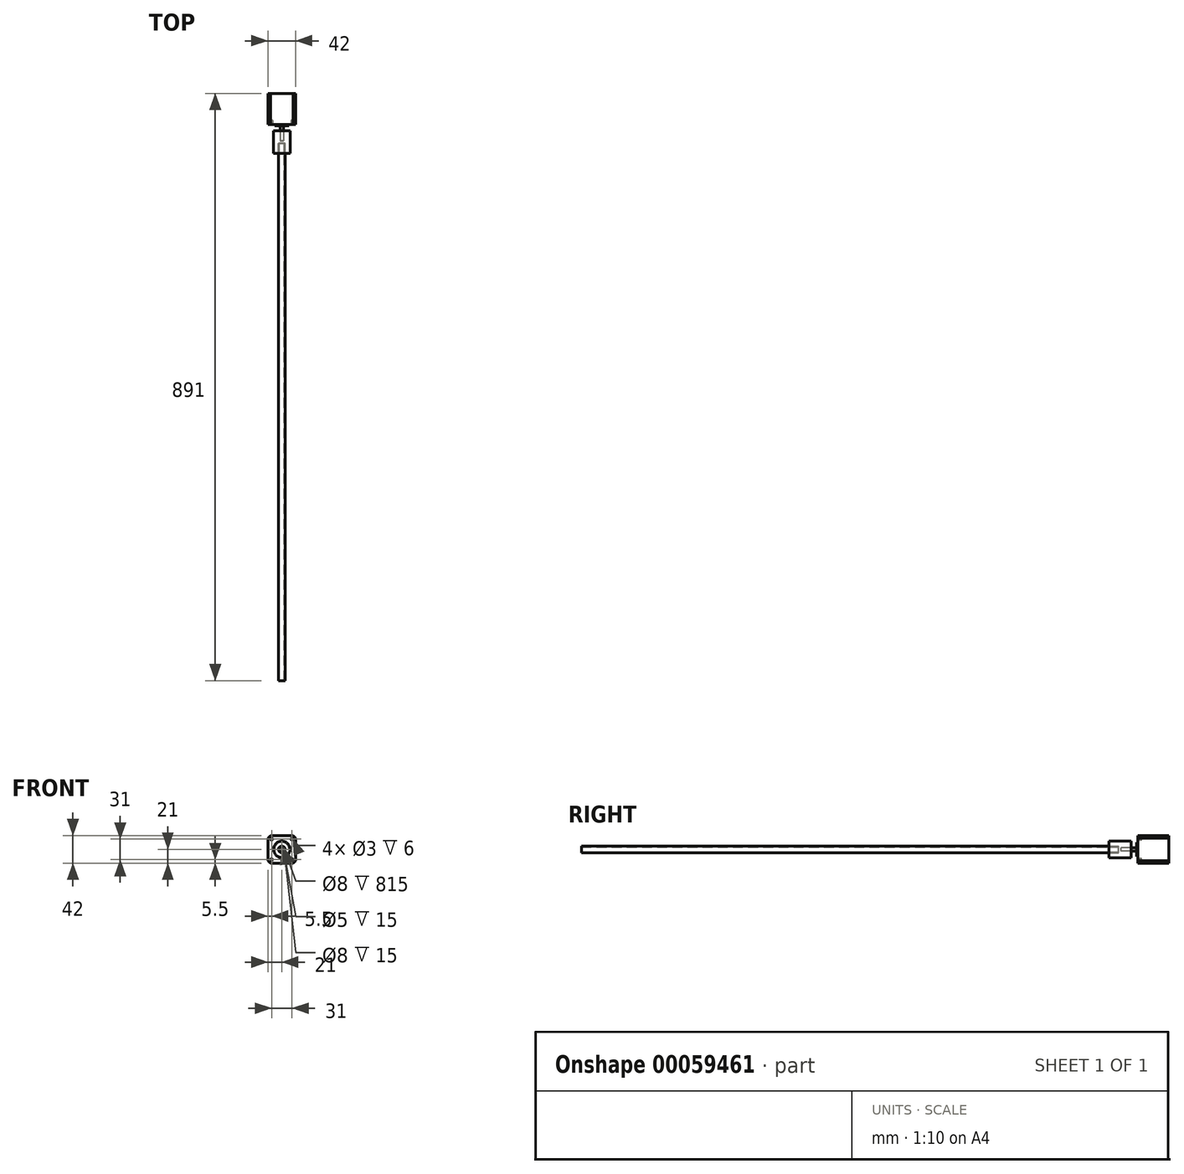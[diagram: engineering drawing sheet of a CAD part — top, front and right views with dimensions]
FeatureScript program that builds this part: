
annotation { "Feature Type Name" : "Feature", "Feature Type Description" : "" }
export const myFeature = defineFeature(function(context is Context, id is Id, definition is map)
    precondition{}
    {
        {
            var Q0;
            Q0=qCreatedBy(makeId("Front.planeOp"),FACE);
            var sketch = newSketch(context, id + "F0", { "sketchPlane" : qUnion([Q0])});
            skLineSegment(sketch, "E0.bottom", {"start": v(-21, -21) * mm, "end": v(21, -21) * mm});
            skLineSegment(sketch, "E0.top", {"start": v(-21, 21) * mm, "end": v(21, 21) * mm});
            skLineSegment(sketch, "E0.left", {"start": v(-21, -21) * mm, "end": v(-21, 21) * mm});
            skLineSegment(sketch, "E0.right", {"start": v(21, -21) * mm, "end": v(21, 21) * mm});
            skCircle(sketch, "E1", {"center": v(0, 0) * mm, "radius": 11 * mm});
            skCircle(sketch, "E2", {"center": v(0, 0) * mm, "radius": 2.5 * mm});
            skSolve(sketch);
        }
        {
            var Q0;
            Q0=makeQuery(id+"F0.imprint","IMPRINT",FACE,{"disambiguationData":[TD([[makeQuery(id+"F0.imprint","IMPRINT",EDGE,{"derivedFrom":sQuery(id+"F0.wireOp",EDGE,"E0.bottom")}),1.0]])]});
            var Q1;
            Q1=makeQuery(id+"F0.imprint","IMPRINT",FACE,{"disambiguationData":[TD([[makeQuery(id+"F0.imprint","IMPRINT",EDGE,{"derivedFrom":sQuery(id+"F0.wireOp",EDGE,"E1")}),1.0]])]});
            var Q2;
            Q2=makeQuery(id+"F0.imprint","IMPRINT",FACE,{"disambiguationData":[TD([[makeQuery(id+"F0.imprint","IMPRINT",EDGE,{"derivedFrom":sQuery(id+"F0.wireOp",EDGE,"E2")}),1.0]])]});
            extrude(context, id + "F1", {"entities" : qUnion([Q0, Q1, Q2]), "oppositeDirection" : true, "depth" : 47 * mm});
        }
        {
            var Q0;
            Q0=makeQuery(id+"F0.imprint","IMPRINT",FACE,{"disambiguationData":[TD([[makeQuery(id+"F0.imprint","IMPRINT",EDGE,{"derivedFrom":sQuery(id+"F0.wireOp",EDGE,"E2")}),1.0]])]});
            var Q1;
            Q1=makeQuery(id+"F0.imprint","IMPRINT",FACE,{"disambiguationData":[TD([[makeQuery(id+"F0.imprint","IMPRINT",EDGE,{"derivedFrom":sQuery(id+"F0.wireOp",EDGE,"E1")}),1.0]])]});
            extrude(context, id + "F2", {"entities" : qUnion([Q0, Q1]), "operationType" : NewBodyOperationType.ADD, "depth" : 2 * mm});
        }
        {
            var Q0;
            Q0=makeQuery(id+"F0.imprint","IMPRINT",FACE,{"disambiguationData":[TD([[makeQuery(id+"F0.imprint","IMPRINT",EDGE,{"derivedFrom":sQuery(id+"F0.wireOp",EDGE,"E2")}),1.0]])]});
            extrude(context, id + "F3", {"entities" : qUnion([Q0]), "operationType" : NewBodyOperationType.ADD, "depth" : 25 * mm});
        }
        {
            var Q0;
            Q0=makeQuery(id+"F1.opExtrude","SWEPT_EDGE",EDGE,{"disambiguationData":[OSD([sQuery(id+"F0.wireOp",EDGE,"E0.top"),sQuery(id+"F0.wireOp",EDGE,"E0.right")])]});
            var Q1;
            Q1=makeQuery(id+"F1.opExtrude","SWEPT_EDGE",EDGE,{"disambiguationData":[OSD([sQuery(id+"F0.wireOp",EDGE,"E0.top"),sQuery(id+"F0.wireOp",EDGE,"E0.left")])]});
            var Q2;
            Q2=makeQuery(id+"F1.opExtrude","SWEPT_EDGE",EDGE,{"disambiguationData":[OSD([sQuery(id+"F0.wireOp",EDGE,"E0.bottom"),sQuery(id+"F0.wireOp",EDGE,"E0.right")])]});
            var Q3;
            Q3=makeQuery(id+"F1.opExtrude","SWEPT_EDGE",EDGE,{"disambiguationData":[OSD([sQuery(id+"F0.wireOp",EDGE,"E0.bottom"),sQuery(id+"F0.wireOp",EDGE,"E0.left")])]});
            chamfer(context, id + "F4", {"entities" : qUnion([Q0, Q1, Q2, Q3]), "width" : 4 * mm, "tangentPropagation" : true});
        }
        {
            var Q0;
            Q0=makeQuery(id+"F0.imprint","IMPRINT",FACE,{"disambiguationData":[TD([[makeQuery(id+"F0.imprint","IMPRINT",EDGE,{"derivedFrom":sQuery(id+"F0.wireOp",EDGE,"E0.bottom")}),1.0]])]});
            var sketch = newSketch(context, id + "F5", { "sketchPlane" : qUnion([Q0])});
            skCircle(sketch, "E3", {"center": v(-15.5, 15.5) * mm, "radius": 1.5 * mm});
            skCircle(sketch, "E4", {"center": v(15.5, 15.5) * mm, "radius": 1.5 * mm});
            skCircle(sketch, "E5", {"center": v(15.5, -15.5) * mm, "radius": 1.5 * mm});
            skCircle(sketch, "E6", {"center": v(-15.5, -15.5) * mm, "radius": 1.5 * mm});
            skSolve(sketch);
        }
        {
            var Q0;
            Q0=makeQuery(id+"F5.imprint","IMPRINT",FACE,{"disambiguationData":[TD([[makeQuery(id+"F5.imprint","IMPRINT",EDGE,{"derivedFrom":sQuery(id+"F5.wireOp",EDGE,"E5")}),1.0]])]});
            var Q1;
            Q1=makeQuery(id+"F5.imprint","IMPRINT",FACE,{"disambiguationData":[TD([[makeQuery(id+"F5.imprint","IMPRINT",EDGE,{"derivedFrom":sQuery(id+"F5.wireOp",EDGE,"E6")}),1.0]])]});
            var Q2;
            Q2=makeQuery(id+"F5.imprint","IMPRINT",FACE,{"disambiguationData":[TD([[makeQuery(id+"F5.imprint","IMPRINT",EDGE,{"derivedFrom":sQuery(id+"F5.wireOp",EDGE,"E3")}),1.0]])]});
            var Q3;
            Q3=makeQuery(id+"F5.imprint","IMPRINT",FACE,{"disambiguationData":[TD([[makeQuery(id+"F5.imprint","IMPRINT",EDGE,{"derivedFrom":sQuery(id+"F5.wireOp",EDGE,"E4")}),1.0]])]});
            extrude(context, id + "F6", {"entities" : qUnion([Q0, Q1, Q2, Q3]), "operationType" : NewBodyOperationType.REMOVE, "oppositeDirection" : true, "depth" : 6 * mm});
        }
        {
            var Q0;
            Q0=makeQuery(id+"F3.opExtrude","CAP_FACE",FACE,{"disambiguationData":[OSD([sQuery(id+"F0.wireOp",EDGE,"E2")])],"isStart":false});
            var sketch = newSketch(context, id + "F7", { "sketchPlane" : qUnion([Q0])});
            skCircle(sketch, "E7", {"center": v(0, 0) * mm, "radius": 12.5 * mm});
            skCircle(sketch, "E8", {"center": v(0, 0) * mm, "radius": 2.5 * mm});
            skCircle(sketch, "E9", {"center": v(0, 0) * mm, "radius": 4 * mm});
            skSolve(sketch);
        }
        {
            var Q0;
            Q0=makeQuery(id+"F7.imprint","IMPRINT",FACE,{"disambiguationData":[TD([[makeQuery(id+"F7.imprint","IMPRINT",EDGE,{"derivedFrom":sQuery(id+"F7.wireOp",EDGE,"E8")}),1.0]])]});
            var Q1;
            Q1=makeQuery(id+"F7.imprint","IMPRINT",FACE,{"disambiguationData":[TD([[makeQuery(id+"F7.imprint","IMPRINT",EDGE,{"derivedFrom":sQuery(id+"F7.wireOp",EDGE,"E7")}),1.0]])]});
            var Q2;
            Q2=makeQuery(id+"F7.imprint","IMPRINT",FACE,{"disambiguationData":[TD([[makeQuery(id+"F7.imprint","IMPRINT",EDGE,{"derivedFrom":sQuery(id+"F7.wireOp",EDGE,"E8")}),-1.0]])]});
            extrude(context, id + "F8", {"entities" : qUnion([Q0, Q1, Q2]), "depth" : 19 * mm, "hasSecondDirection" : true, "secondDirectionOppositeDirection" : true, "secondDirectionDepth" : 15 * mm});
        }
        {
            var Q0;
            Q0=makeQuery(id+"F7.imprint","IMPRINT",FACE,{"disambiguationData":[TD([[makeQuery(id+"F7.imprint","IMPRINT",EDGE,{"derivedFrom":sQuery(id+"F7.wireOp",EDGE,"E8")}),1.0]])]});
            extrude(context, id + "F9", {"entities" : qUnion([Q0]), "operationType" : NewBodyOperationType.REMOVE, "oppositeDirection" : true, "depth" : 15 * mm});
        }
        {
            var Q0;
            Q0=makeQuery(id+"F7.imprint","IMPRINT",FACE,{"disambiguationData":[TD([[makeQuery(id+"F7.imprint","IMPRINT",EDGE,{"derivedFrom":sQuery(id+"F7.wireOp",EDGE,"E8")}),-1.0]])]});
            var Q1;
            Q1=makeQuery(id+"F7.imprint","IMPRINT",FACE,{"disambiguationData":[TD([[makeQuery(id+"F7.imprint","IMPRINT",EDGE,{"derivedFrom":sQuery(id+"F7.wireOp",EDGE,"E8")}),1.0]])]});
            extrude(context, id + "F10", {"entities" : qUnion([Q0, Q1]), "operationType" : NewBodyOperationType.REMOVE, "depth" : 19 * mm, "hasSecondDirection" : true, "secondDirectionOppositeDirection" : false, "secondDirectionDepth" : 4 * mm});
        }
        {
            var Q0;
            Q0=makeQuery(id+"F8.opExtrude","CAP_FACE",FACE,{"disambiguationData":[OSD([sQuery(id+"F7.wireOp",EDGE,"E7")])],"isStart":false});
            var sketch = newSketch(context, id + "F11", { "sketchPlane" : qUnion([Q0])});
            skCircle(sketch, "E10", {"center": v(0, 0) * mm, "radius": 5 * mm});
            skSolve(sketch);
        }
        {
            var Q0;
            Q0=makeQuery(id+"F11.imprint","IMPRINT",FACE,{"disambiguationData":[TD([[makeQuery(id+"F11.imprint","IMPRINT",EDGE,{"derivedFrom":sQuery(id+"F11.wireOp",EDGE,"E10")}),1.0]])]});
            var Q1;
            Q1=makeQuery(id+"F11.imprint","IMPRINT",FACE,{"disambiguationData":[TD([[makeQuery(id+"F11.imprint","IMPRINT",EDGE,{"derivedFrom":makeQuery(id+"F10.boolean.opBoolean","COPY",EDGE,{"derivedFrom":makeQuery(id+"F10.opExtrude","CAP_EDGE",EDGE,{"disambiguationData":[OSD([sQuery(id+"F7.wireOp",EDGE,"E9")])],"isStart":false})})}),1.0]])]});
            extrude(context, id + "F12", {"entities" : qUnion([Q0, Q1]), "depth" : 800 * mm, "hasSecondDirection" : true, "secondDirectionOppositeDirection" : true, "secondDirectionDepth" : 15 * mm});
        }
    });
